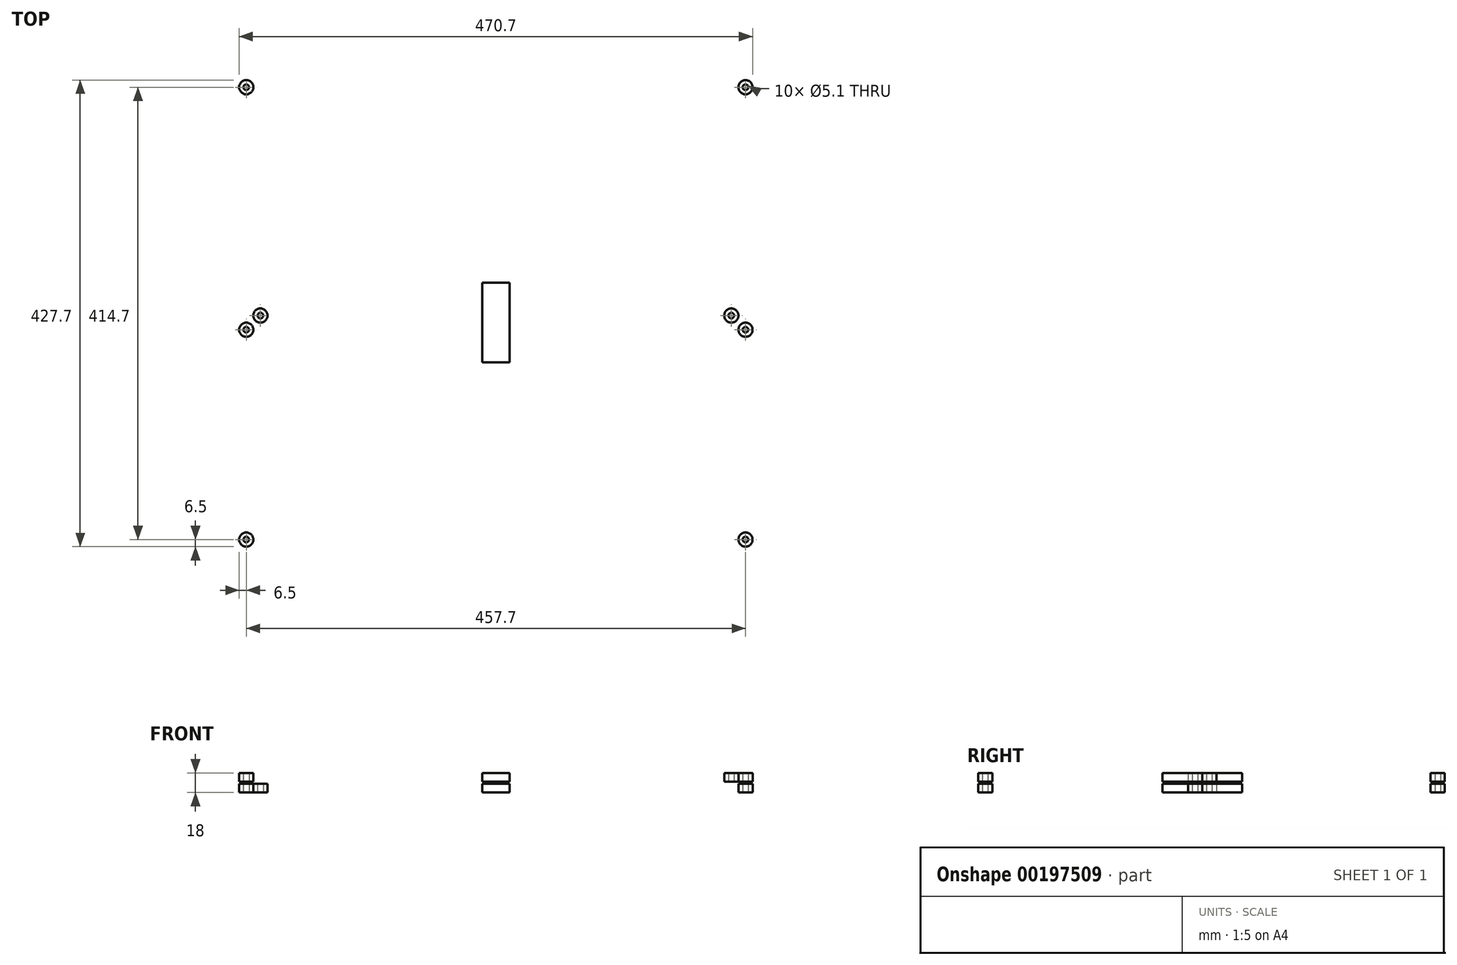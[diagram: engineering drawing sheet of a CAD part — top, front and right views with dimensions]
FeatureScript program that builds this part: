
annotation { "Feature Type Name" : "Feature", "Feature Type Description" : "" }
export const myFeature = defineFeature(function(context is Context, id is Id, definition is map)
    precondition{}
    {
        {
            var Q0;
            Q0=qCreatedBy(makeId("Top.planeOp"),FACE);
            var sketch = newSketch(context, id + "F0", { "sketchPlane" : qUnion([Q0])});
            skLineSegment(sketch, "E0.right", {"start": v(250, 260) * mm, "end": v(250, 240) * mm});
            skLineSegment(sketch, "E1.bottom", {"start": v(-250, -240) * mm, "end": v(250, -240) * mm});
            skLineSegment(sketch, "E1.top", {"start": v(-250, -220) * mm, "end": v(250, -220) * mm});
            skLineSegment(sketch, "E1.right", {"start": v(250, -240) * mm, "end": v(250, -220) * mm});
            skLineSegment(sketch, "E2.bottom", {"start": v(250, 240) * mm, "end": v(270, 240) * mm});
            skLineSegment(sketch, "E2.top", {"start": v(250, -220) * mm, "end": v(270, -220) * mm});
            skLineSegment(sketch, "E2.left", {"start": v(250, 240) * mm, "end": v(250, -220) * mm});
            skLineSegment(sketch, "E2.right", {"start": v(270, 240) * mm, "end": v(270, -220) * mm});
            skLineSegment(sketch, "E3.bottom", {"start": v(250, 240) * mm, "end": v(-250, 240) * mm});
            skLineSegment(sketch, "E3.top", {"start": v(250, 260) * mm, "end": v(-250, 260) * mm});
            skLineSegment(sketch, "E3.left", {"start": v(250, 240) * mm, "end": v(250, 260) * mm});
            skLineSegment(sketch, "E3.right", {"start": v(-250, 240) * mm, "end": v(-250, 260) * mm});
            skLineSegment(sketch, "E4.bottom", {"start": v(-250, -220) * mm, "end": v(-270, -220) * mm});
            skLineSegment(sketch, "E4.top", {"start": v(-250, 240) * mm, "end": v(-270, 240) * mm});
            skLineSegment(sketch, "E4.left", {"start": v(-250, -220) * mm, "end": v(-250, 240) * mm});
            skLineSegment(sketch, "E4.right", {"start": v(-270, -220) * mm, "end": v(-270, 240) * mm});
            skLineSegment(sketch, "E5", {"start": v(-250, -240) * mm, "end": v(-250, -220) * mm});
            skLineSegment(sketch, "E6.bottom", {"start": v(-270, -220) * mm, "end": v(-250, -220) * mm});
            skLineSegment(sketch, "E6.top", {"start": v(-270, -240) * mm, "end": v(-250, -240) * mm});
            skLineSegment(sketch, "E6.left", {"start": v(-270, -220) * mm, "end": v(-270, -240) * mm});
            skLineSegment(sketch, "E6.right", {"start": v(-250, -220) * mm, "end": v(-250, -240) * mm});
            skLineSegment(sketch, "E7.top", {"start": v(250, -240) * mm, "end": v(270, -240) * mm});
            skLineSegment(sketch, "E7.left", {"start": v(250, -220) * mm, "end": v(250, -240) * mm});
            skLineSegment(sketch, "E7.right", {"start": v(270, -220) * mm, "end": v(270, -240) * mm});
            skLineSegment(sketch, "E8.bottom", {"start": v(250, 260) * mm, "end": v(270, 260) * mm});
            skLineSegment(sketch, "E8.right", {"start": v(270, 260) * mm, "end": v(270, 240) * mm});
            skLineSegment(sketch, "E9.bottom", {"start": v(-250, 260) * mm, "end": v(-270, 260) * mm});
            skLineSegment(sketch, "E9.left", {"start": v(-250, 260) * mm, "end": v(-250, 240) * mm});
            skLineSegment(sketch, "E9.right", {"start": v(-270, 260) * mm, "end": v(-270, 240) * mm});
            skSolve(sketch);
        }
        {
            var Q0;
            Q0=qCreatedBy(makeId("Top.planeOp"),FACE);
            var sketch = newSketch(context, id + "F1", { "sketchPlane" : qUnion([Q0])});
            skPoint(sketch, "E10.0", {"position": v(-250, 240) * mm});
            skLineSegment(sketch, "E11.top", {"start": v(-250, 194.7) * mm, "end": v(-207.7, 194.7) * mm});
            skLineSegment(sketch, "E11.left", {"start": v(-250, 237) * mm, "end": v(-250, 194.7) * mm});
            skCircle(sketch, "E12", {"center": v(-228.85, 215.85) * mm, "radius": 11 * mm});
            skCircle(sketch, "E13", {"center": v(-228.85, 215.85) * mm, "radius": 2.5 * mm});
            skLineSegment(sketch, "E14", {"start": v(-207.7, 194.7) * mm, "end": v(-207.7, 237) * mm});
            skLineSegment(sketch, "E15", {"start": v(-207.7, 237) * mm, "end": v(-250, 237) * mm});
            skPoint(sketch, "E16.0", {"position": v(207.7, 211.72) * mm});
            skLineSegment(sketch, "E17.top", {"start": v(207.7, 194.7) * mm, "end": v(250, 194.7) * mm});
            skLineSegment(sketch, "E17.left", {"start": v(207.7, 237) * mm, "end": v(207.7, 194.7) * mm});
            skCircle(sketch, "E18", {"center": v(228.85, 215.85) * mm, "radius": 11 * mm});
            skCircle(sketch, "E19", {"center": v(228.85, 215.85) * mm, "radius": 2.5 * mm});
            skLineSegment(sketch, "E20", {"start": v(250, 194.7) * mm, "end": v(250, 237) * mm});
            skLineSegment(sketch, "E21", {"start": v(250, 237) * mm, "end": v(207.7, 237) * mm});
            skSolve(sketch);
        }
        {
            var Q0;
            Q0=qCreatedBy(makeId("Top.planeOp"),FACE);
            var sketch = newSketch(context, id + "F2", { "sketchPlane" : qUnion([Q0])});
            skLineSegment(sketch, "E22.0", {"start": v(-250, 240) * mm, "end": v(-250, 260) * mm});
            skLineSegment(sketch, "E23.0", {"start": v(-250, 240) * mm, "end": v(-270, 240) * mm});
            skLineSegment(sketch, "E24", {"start": v(-250, 260) * mm, "end": v(-207.7, 260) * mm});
            skCircle(sketch, "E25", {"center": v(-228.85, 215.85) * mm, "radius": 12 * mm});
            skLineSegment(sketch, "E26.0", {"start": v(250, 240) * mm, "end": v(250, 260) * mm});
            skLineSegment(sketch, "E27.0", {"start": v(250, 240) * mm, "end": v(270, 240) * mm});
            skLineSegment(sketch, "E28.0", {"start": v(207.7, 260) * mm, "end": v(207.7, 185.7) * mm});
            skLineSegment(sketch, "E29", {"start": v(250, 260) * mm, "end": v(207.7, 260) * mm});
            skLineSegment(sketch, "E30", {"start": v(270, 185.7) * mm, "end": v(270, 240) * mm});
            skPoint(sketch, "E31.0", {"position": v(228.85, 215.85) * mm});
            skCircle(sketch, "E32", {"center": v(228.85, 215.85) * mm, "radius": 12 * mm});
            skCircle(sketch, "E33.0", {"center": v(228.85, 215.85) * mm, "radius": 11 * mm, "construction": true});
            skCircle(sketch, "E34", {"center": v(228.85, 250) * mm, "radius": 2.65 * mm});
            skPoint(sketch, "E34.centerSnap0", {"position": v(228.85, 260) * mm});
            skPoint(sketch, "E34.centerSnap1", {"position": v(207.7, 250) * mm});
            skCircle(sketch, "E35", {"center": v(-260, 225) * mm, "radius": 2.65 * mm});
            skCircle(sketch, "E36", {"center": v(-228.85, 250) * mm, "radius": 2.65 * mm});
            skPoint(sketch, "E36.centerSnap0", {"position": v(-228.85, 260) * mm});
            skPoint(sketch, "E36.centerSnap1", {"position": v(-250, 250) * mm});
            skLineSegment(sketch, "E37.left", {"start": v(-270, 240) * mm, "end": v(-270, 185.7) * mm});
            skLineSegment(sketch, "E37.right", {"start": v(-207.7, 260) * mm, "end": v(-207.7, 185.7) * mm});
            skCircle(sketch, "E38", {"center": v(-260, 205.7) * mm, "radius": 2.65 * mm});
            skCircle(sketch, "E39", {"center": v(260, 225) * mm, "radius": 2.65 * mm});
            skPoint(sketch, "E39.centerSnap0", {"position": v(260, 240) * mm});
            skCircle(sketch, "E40", {"center": v(260, 205.7) * mm, "radius": 2.65 * mm});
            skLineSegment(sketch, "E41", {"start": v(-270, 185.7) * mm, "end": v(-207.7, 185.7) * mm});
            skPoint(sketch, "E42.orphan", {"position": v(-207.7, 240) * mm});
            skLineSegment(sketch, "E43", {"start": v(207.7, 185.7) * mm, "end": v(270, 185.7) * mm});
            skSolve(sketch);
        }
        {
            var Q0;
            Q0=qCreatedBy(makeId("Top.planeOp"),FACE);
            var sketch = newSketch(context, id + "F3", { "sketchPlane" : qUnion([Q0])});
            skPoint(sketch, "E44.0", {"position": v(-270, -240) * mm});
            skLineSegment(sketch, "E45.bottom", {"start": v(-250, -240) * mm, "end": v(-207.7, -240) * mm});
            skLineSegment(sketch, "E45.top", {"start": v(-270, -177.7) * mm, "end": v(-207.7, -177.7) * mm});
            skLineSegment(sketch, "E45.left", {"start": v(-270, -220) * mm, "end": v(-270, -177.7) * mm});
            skLineSegment(sketch, "E45.right", {"start": v(-207.7, -240) * mm, "end": v(-207.7, -177.7) * mm});
            skPoint(sketch, "E46.0", {"position": v(-250, -220) * mm});
            skLineSegment(sketch, "E47", {"start": v(-250, -220) * mm, "end": v(-270, -220) * mm});
            skLineSegment(sketch, "E48", {"start": v(-250, -220) * mm, "end": v(-250, -240) * mm});
            skPoint(sketch, "E49.0", {"position": v(270, -240) * mm});
            skPoint(sketch, "E49.1", {"position": v(250, -220) * mm});
            skLineSegment(sketch, "E50.bottom", {"start": v(250, -240) * mm, "end": v(207.7, -240) * mm});
            skLineSegment(sketch, "E50.top", {"start": v(270, -177.7) * mm, "end": v(207.7, -177.7) * mm});
            skLineSegment(sketch, "E50.left", {"start": v(270, -220) * mm, "end": v(270, -177.7) * mm});
            skLineSegment(sketch, "E50.right", {"start": v(207.7, -240) * mm, "end": v(207.7, -177.7) * mm});
            skLineSegment(sketch, "E51", {"start": v(250, -220) * mm, "end": v(270, -220) * mm});
            skLineSegment(sketch, "E52", {"start": v(270, -220) * mm, "end": v(250, -220) * mm});
            skLineSegment(sketch, "E53", {"start": v(250, -220) * mm, "end": v(250, -240) * mm});
            skCircle(sketch, "E54", {"center": v(-228.85, -198.85) * mm, "radius": 2.65 * mm});
            skPoint(sketch, "E54.centerSnap0", {"position": v(-228.85, -240) * mm});
            skCircle(sketch, "E55", {"center": v(228.85, -198.85) * mm, "radius": 2.65 * mm});
            skPoint(sketch, "E55.centerSnap0", {"position": v(228.85, -240) * mm});
            skCircle(sketch, "E56", {"center": v(-260, -198.85) * mm, "radius": 2.65 * mm});
            skPoint(sketch, "E56.centerSnap0", {"position": v(-270, -198.85) * mm});
            skPoint(sketch, "E56.centerSnap1", {"position": v(-260, -220) * mm});
            skCircle(sketch, "E57", {"center": v(-228.85, -230) * mm, "radius": 2.65 * mm});
            skPoint(sketch, "E57.centerSnap0", {"position": v(-250, -230) * mm});
            skCircle(sketch, "E58", {"center": v(228.85, -230) * mm, "radius": 2.65 * mm});
            skPoint(sketch, "E58.centerSnap0", {"position": v(250, -230) * mm});
            skCircle(sketch, "E59", {"center": v(260, -198.85) * mm, "radius": 2.65 * mm});
            skPoint(sketch, "E59.centerSnap0", {"position": v(270, -198.85) * mm});
            skPoint(sketch, "E59.centerSnap1", {"position": v(260, -220) * mm});
            skSolve(sketch);
        }
        {
            var Q0;
            Q0=qCreatedBy(makeId("Top.planeOp"),FACE);
            var sketch = newSketch(context, id + "F4", { "sketchPlane" : qUnion([Q0])});
            skCircle(sketch, "E60", {"center": v(-228.85, 215.85) * mm, "radius": 6.5 * mm});
            skCircle(sketch, "E61", {"center": v(-228.85, -198.85) * mm, "radius": 6.5 * mm});
            skCircle(sketch, "E62", {"center": v(228.85, -198.85) * mm, "radius": 6.5 * mm});
            skCircle(sketch, "E63", {"center": v(-228.85, 215.85) * mm, "radius": 2.55 * mm});
            skCircle(sketch, "E64", {"center": v(-228.85, -198.85) * mm, "radius": 2.55 * mm});
            skCircle(sketch, "E65", {"center": v(228.85, -198.85) * mm, "radius": 2.55 * mm});
            skLineSegment(sketch, "E66", {"start": v(228.85, -205.35) * mm, "end": v(-228.85, -205.35) * mm, "construction": true});
            skLineSegment(sketch, "E67", {"start": v(-235.35, -198.85) * mm, "end": v(-235.35, 215.85) * mm, "construction": true});
            skLineSegment(sketch, "E68", {"start": v(-222.35, 215.85) * mm, "end": v(-222.35, 6.5) * mm, "construction": true});
            skLineSegment(sketch, "E69.bottom", {"start": v(-12.5, 36.5) * mm, "end": v(12.5, 36.5) * mm});
            skLineSegment(sketch, "E69.top", {"start": v(-12.5, -36.5) * mm, "end": v(12.5, -36.5) * mm});
            skLineSegment(sketch, "E69.left", {"start": v(-12.5, 36.5) * mm, "end": v(-12.5, -36.5) * mm});
            skLineSegment(sketch, "E69.right", {"start": v(12.5, 36.5) * mm, "end": v(12.5, -36.5) * mm});
            skCircle(sketch, "E70", {"center": v(-215.85, 6.5) * mm, "radius": 6.5 * mm});
            skCircle(sketch, "E71", {"center": v(-215.85, 6.5) * mm, "radius": 2.55 * mm});
            skLineSegment(sketch, "E72", {"start": v(-215.85, 0) * mm, "end": v(-12.5, 0) * mm, "construction": true});
            skCircle(sketch, "E73", {"center": v(228.85, -6.5) * mm, "radius": 6.5 * mm});
            skCircle(sketch, "E74", {"center": v(228.85, -6.5) * mm, "radius": 2.55 * mm});
            skLineSegment(sketch, "E75", {"start": v(235.35, -198.85) * mm, "end": v(235.35, -6.5) * mm, "construction": true});
            skLineSegment(sketch, "E76", {"start": v(12.5, 0) * mm, "end": v(228.85, 0) * mm, "construction": true});
            skSolve(sketch);
        }
        {
            var Q0;
            Q0=qSketchRegion(id+"F4",true);
            extrude(context, id + "F5", {"entities" : qUnion([Q0]), "depth" : 8 * mm});
        }
        {
            var Q0;
            Q0=makeQuery(id+"F5.opExtrude","CAP_FACE",FACE,{"disambiguationData":[OSD([sQuery(id+"F4.wireOp",EDGE,"E69.bottom"),sQuery(id+"F4.wireOp",EDGE,"E69.top"),sQuery(id+"F4.wireOp",EDGE,"E69.left"),sQuery(id+"F4.wireOp",EDGE,"E69.right")])],"isStart":false});
            cPlane(context, id + "F6", {"entities" : qUnion([Q0]), "cplaneType" : CPlaneType.OFFSET, "offset" : 2 * mm, "width" : 150 * mm, "height" : 150 * mm});
        }
        {
            var Q0;
            Q0=qCreatedBy(id+"F6.planeOp",FACE);
            var sketch = newSketch(context, id + "F7", { "sketchPlane" : qUnion([Q0])});
            skCircle(sketch, "E77.1", {"center": v(228.85, 215.85) * mm, "radius": 6.5 * mm});
            skCircle(sketch, "E77.4", {"center": v(-228.85, -198.85) * mm, "radius": 6.5 * mm});
            skCircle(sketch, "E77.5", {"center": v(228.85, -198.85) * mm, "radius": 6.5 * mm});
            skCircle(sketch, "E78.2", {"center": v(-228.85, -198.85) * mm, "radius": 2.55 * mm});
            skCircle(sketch, "E78.3", {"center": v(228.85, -198.85) * mm, "radius": 2.55 * mm});
            skCircle(sketch, "E78.5", {"center": v(228.85, 215.85) * mm, "radius": 2.55 * mm});
            skLineSegment(sketch, "E79.0", {"start": v(-12.5, 36.5) * mm, "end": v(-12.5, -36.5) * mm});
            skLineSegment(sketch, "E80.0", {"start": v(-12.5, 36.5) * mm, "end": v(12.5, 36.5) * mm});
            skLineSegment(sketch, "E81.0", {"start": v(12.5, 36.5) * mm, "end": v(12.5, -36.5) * mm});
            skLineSegment(sketch, "E82.0", {"start": v(-12.5, -36.5) * mm, "end": v(12.5, -36.5) * mm});
            skCircle(sketch, "E83", {"center": v(-228.85, -6.5) * mm, "radius": 6.5 * mm});
            skCircle(sketch, "E84", {"center": v(-228.85, -6.5) * mm, "radius": 2.55 * mm});
            skCircle(sketch, "E85", {"center": v(215.85, 6.5) * mm, "radius": 6.5 * mm});
            skCircle(sketch, "E86", {"center": v(215.85, 6.5) * mm, "radius": 2.55 * mm});
            skLineSegment(sketch, "E87", {"start": v(222.35, 215.85) * mm, "end": v(222.35, 6.5) * mm, "construction": true});
            skLineSegment(sketch, "E88", {"start": v(215.85, 0) * mm, "end": v(12.5, 0) * mm, "construction": true});
            skLineSegment(sketch, "E89", {"start": v(235.35, 215.85) * mm, "end": v(235.35, -198.85) * mm, "construction": true});
            skLineSegment(sketch, "E90", {"start": v(-228.85, -205.35) * mm, "end": v(228.85, -205.35) * mm, "construction": true});
            skLineSegment(sketch, "E91", {"start": v(-235.35, -198.85) * mm, "end": v(-235.35, -6.5) * mm, "construction": true});
            skLineSegment(sketch, "E92", {"start": v(-228.85, 0) * mm, "end": v(-12.5, 0) * mm, "construction": true});
            skSolve(sketch);
        }
        {
            var Q0;
            Q0=qSketchRegion(id+"F7",true);
            extrude(context, id + "F8", {"entities" : qUnion([Q0]), "depth" : 8 * mm});
        }
    });
